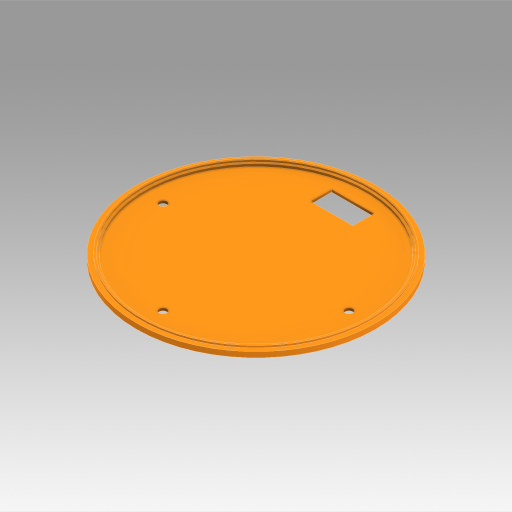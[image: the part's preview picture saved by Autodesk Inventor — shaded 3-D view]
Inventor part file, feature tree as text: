
AUTODESK INVENTOR PART (.ipt)
format: ipt  version: 2023 (Build 270158000, 158)  size: 218,112 bytes
history: native  units: mm
features: extrude x5, sketch x3, projected_geometry x1
ambient origin geometry x8: Origin, YZ Plane, XZ Plane, XY Plane, X Axis, Y Axis, Z Axis, Center Point
bodies: Solid1 (feature_tree)
feature tree (9):
  extrude  "Extrusion1"  Depth=2.0mm TaperAngle=0.0deg
  sketch  "Sketch2"  dims[d3=2.5mm d4=0.75mm]
  extrude  "Extrusion2"  Depth=0.75mm
  extrude  "Extrusion3"  Depth=1.0mm TaperAngle=0.0deg
  sketch  "Sketch3"  dims[d5=0.75mm d6=1.0mm d7=0.0mm d8=0.75mm d9=0.0mm d10=80.0mm d11=5.0mm d12=3.0mm d13=3.0mm d14=5.0mm d15=3.0mm d16=5.0mm d17=16.0mm d18=8.0mm d21=36.45mm d24=0.0mm d25=0.0mm d26=0.0mm d27=0.0mm]
  extrude  "Extrusion5"  Depth=0.75mm TaperAngle=0.0deg
  extrude  "Extrusion6"  Depth=8.0mm
  sketch  "Sketch1"  dims[d0=90.0mm d1=2.0mm d2=0.0mm]
  projected_geometry  "Projected Loop1"
